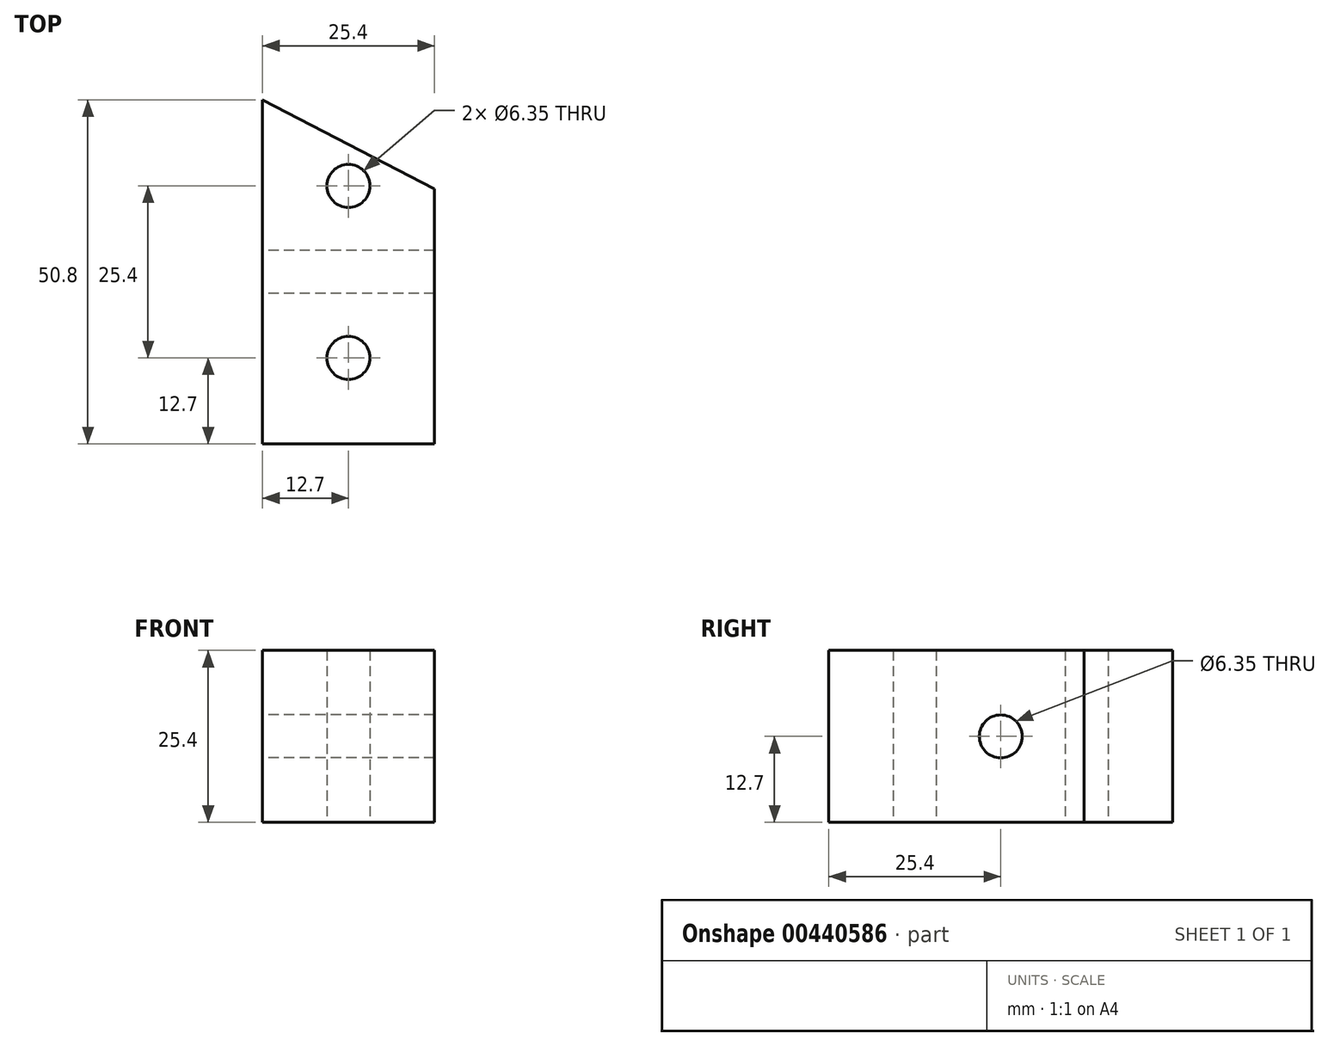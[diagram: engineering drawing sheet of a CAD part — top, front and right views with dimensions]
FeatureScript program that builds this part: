
annotation { "Feature Type Name" : "Feature", "Feature Type Description" : "" }
export const myFeature = defineFeature(function(context is Context, id is Id, definition is map)
    precondition{}
    {
        {
            var Q0;
            Q0=qCreatedBy(makeId("Top.planeOp"),FACE);
            var sketch = newSketch(context, id + "F0", { "sketchPlane" : qUnion([Q0])});
            skLineSegment(sketch, "E0", {"start": v(-12.7, 25.4) * mm, "end": v(-12.7, -25.4) * mm});
            skLineSegment(sketch, "E1", {"start": v(-12.7, -25.4) * mm, "end": v(12.7, -25.4) * mm});
            skLineSegment(sketch, "E2", {"start": v(12.7, -25.4) * mm, "end": v(12.7, 12.3) * mm});
            skLineSegment(sketch, "E3", {"start": v(12.7, 12.3) * mm, "end": v(-12.7, 25.4) * mm});
            skPoint(sketch, "E4", {"position": v(0, -25.4) * mm});
            skCircle(sketch, "E5", {"center": v(0, 12.7) * mm, "radius": 3.18 * mm});
            skCircle(sketch, "E6", {"center": v(0, -12.7) * mm, "radius": 3.18 * mm});
            skPoint(sketch, "E7", {"position": v(-12.7, 0) * mm});
            skSolve(sketch);
        }
        {
            var Q0;
            Q0=makeQuery(id+"F0.imprint","IMPRINT",FACE,{"disambiguationData":[TD([[makeQuery(id+"F0.imprint","IMPRINT",EDGE,{"derivedFrom":sQuery(id+"F0.wireOp",EDGE,"E0")}),1.0]])]});
            extrude(context, id + "F1", {"entities" : qUnion([Q0]), "depth" : 25.4 * mm});
        }
        {
            var Q0;
            Q0=makeQuery(id+"F1.opExtrude","SWEPT_FACE",FACE,{"disambiguationData":[OSD([sQuery(id+"F0.wireOp",EDGE,"E0")])]});
            var sketch = newSketch(context, id + "F2", { "sketchPlane" : qUnion([Q0])});
            skCircle(sketch, "E8", {"center": v(0, 12.7) * mm, "radius": 3.17 * mm});
            skPoint(sketch, "E8.centerSnap0", {"position": v(-25.4, 12.7) * mm});
            skSolve(sketch);
        }
        {
            var Q0;
            Q0=makeQuery(id+"F2.imprint","IMPRINT",FACE,{"disambiguationData":[TD([[makeQuery(id+"F2.imprint","IMPRINT",EDGE,{"derivedFrom":sQuery(id+"F2.wireOp",EDGE,"E8")}),1.0]])]});
            extrude(context, id + "F3", {"entities" : qUnion([Q0]), "operationType" : NewBodyOperationType.REMOVE, "endBound" : BoundingType.UP_TO_NEXT, "oppositeDirection" : true, "depth" : 25.4 * mm});
        }
    });
